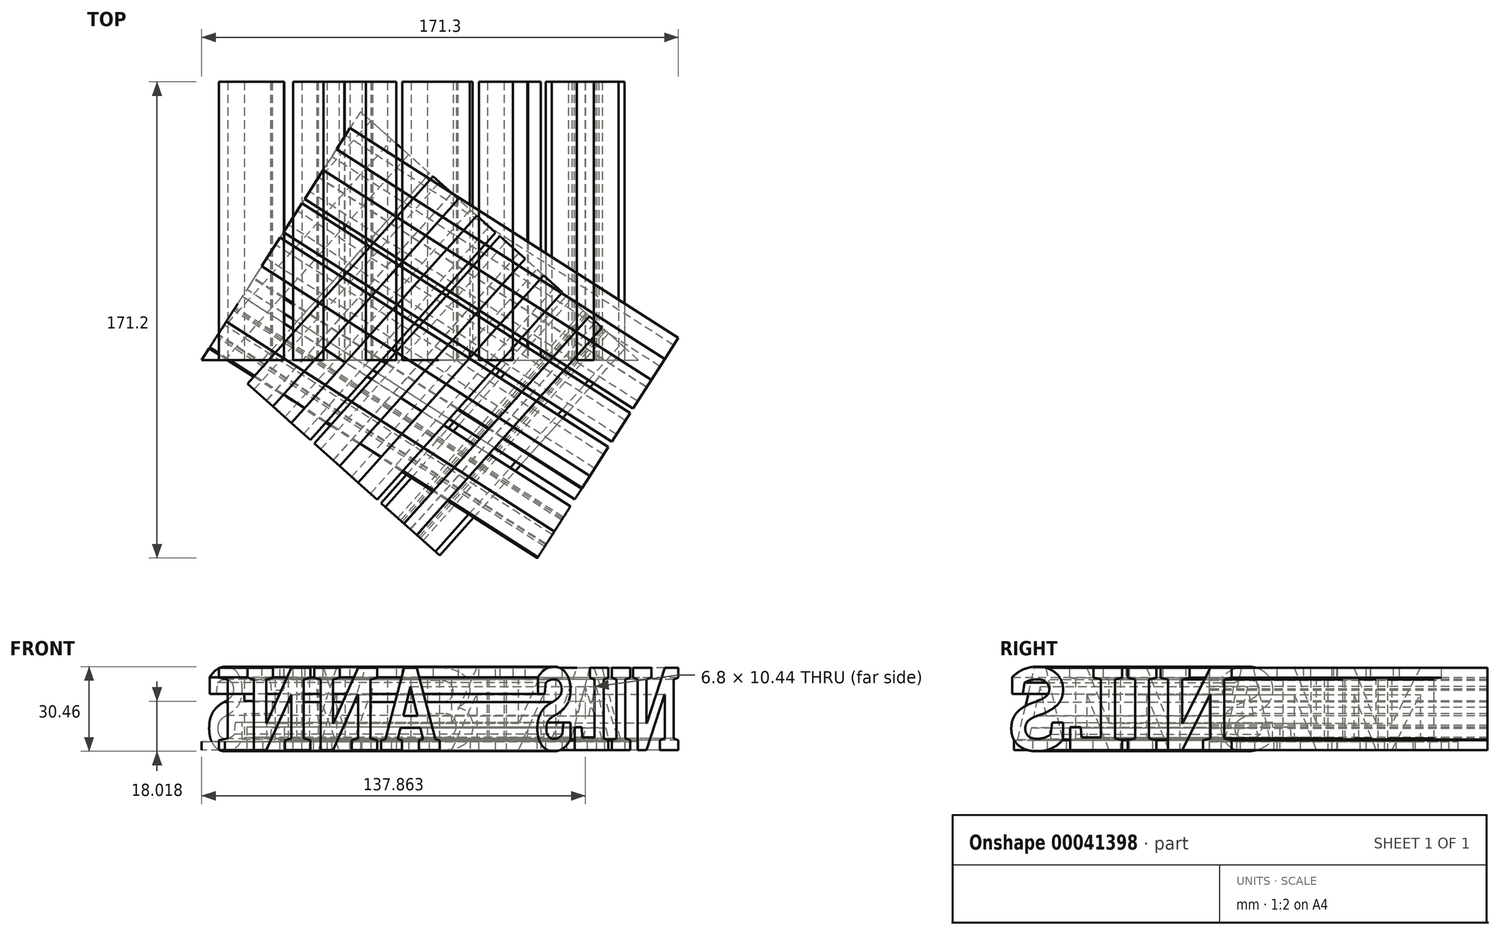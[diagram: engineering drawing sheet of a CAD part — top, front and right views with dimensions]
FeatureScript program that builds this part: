
annotation { "Feature Type Name" : "Feature", "Feature Type Description" : "" }
export const myFeature = defineFeature(function(context is Context, id is Id, definition is map)
    precondition{}
    {
        {
            var Q0;
            Q0=qCreatedBy(makeId("Top.planeOp"),FACE);
            var sketch = newSketch(context, id + "F0", { "sketchPlane" : qUnion([Q0])});
            skLineSegment(sketch, "E0", {"start": v(0, 89.3) * mm, "end": v(-57.1, 0) * mm});
            skLineSegment(sketch, "E1", {"start": v(-57.1, 0) * mm, "end": v(99.9, 0) * mm});
            skLineSegment(sketch, "E2", {"start": v(99.9, 0) * mm, "end": v(0, 89.3) * mm});
            skSolve(sketch);
        }
        {
            var Q0;
            Q0=makeQuery(id+"F0.imprint","IMPRINT",FACE,{"disambiguationData":[TD([[makeQuery(id+"F0.imprint","IMPRINT",EDGE,{"derivedFrom":sQuery(id+"F0.wireOp",EDGE,"E0")}),1.0]])]});
            extrude(context, id + "F1", {"entities" : qUnion([Q0]), "depth" : 3 * mm});
        }
        {
            var Q0;
            Q0=makeQuery(id+"F1.opExtrude","SWEPT_FACE",FACE,{"disambiguationData":[OSD([sQuery(id+"F0.wireOp",EDGE,"E1")])]});
            var sketch = newSketch(context, id + "F2", { "sketchPlane" : qUnion([Q0])});
            skText(sketch, "E3", { "text": "EMBLA", "fontName": "RobotoSlab-Bold.ttf"});
            const initialGuessF2  = {"E3": [-0.05203, 0, 1, 0, 0.03]};
            skSetInitialGuess(sketch, initialGuessF2);
            skSolve(sketch);
        }
        {
            var Q0;
            Q0=makeQuery(id+"F1.opExtrude","SWEPT_FACE",FACE,{"disambiguationData":[OSD([sQuery(id+"F0.wireOp",EDGE,"E2")])]});
            var sketch = newSketch(context, id + "F3", { "sketchPlane" : qUnion([Q0])});
            skText(sketch, "E4", { "text": "ANNA", "fontName": "RobotoSlab-Bold.ttf"});
            const initialGuessF3  = {"E4": [-0.0689, 0, 1, 0, 0.03]};
            skSetInitialGuess(sketch, initialGuessF3);
            skSolve(sketch);
        }
        {
            var Q0;
            Q0=makeQuery(id+"F1.opExtrude","SWEPT_FACE",FACE,{"disambiguationData":[OSD([sQuery(id+"F0.wireOp",EDGE,"E0")])]});
            var sketch = newSketch(context, id + "F4", { "sketchPlane" : qUnion([Q0])});
            skText(sketch, "E5", { "text": "NILS", "fontName": "RobotoSlab-Bold.ttf"});
            const initialGuessF4  = {"E5": [-0.06942, 0, 1, 0, 0.03]};
            skSetInitialGuess(sketch, initialGuessF4);
            skSolve(sketch);
        }
        {
            var Q0;
            Q0 = qSketchRegion(id + "F2", true);
            extrude(context, id + "F5", {"entities" : qUnion([Q0]), "oppositeDirection" : true, "depth" : 100 * mm});
        }
        {
            var Q0;
            Q0 = qSketchRegion(id + "F3", true);
            extrude(context, id + "F6", {"entities" : qUnion([Q0]), "oppositeDirection" : true, "depth" : 100 * mm});
        }
        {
            var Q0;
            Q0 = qSketchRegion(id + "F4", true);
            extrude(context, id + "F7", {"entities" : qUnion([Q0]), "oppositeDirection" : true, "depth" : 140 * mm});
        }
        {
            var Q0;
            Q0=makeQuery(id+"F0.imprint","IMPRINT",FACE,{"disambiguationData":[TD([[makeQuery(id+"F0.imprint","IMPRINT",EDGE,{"derivedFrom":sQuery(id+"F0.wireOp",EDGE,"E0")}),1.0]])]});
            extrude(context, id + "F8", {"entities" : qUnion([Q0]), "depth" : 3 * mm});
        }
        {
            var Q0;
            Q0=makeQuery(id+"F0.imprint","IMPRINT",FACE,{"disambiguationData":[TD([[makeQuery(id+"F0.imprint","IMPRINT",EDGE,{"derivedFrom":sQuery(id+"F0.wireOp",EDGE,"E0")}),1.0]])]});
            extrude(context, id + "F9", {"entities" : qUnion([Q0]), "depth" : 3 * mm});
        }
        {
            var Q0;
            Q0=makeQuery(id+"F6.opExtrude","SWEPT_BODY",BODY,{"disambiguationData":[OSD([sQuery(id+"F3.wireOp",EDGE,"E4.sketch_text.stroke-68"),sQuery(id+"F3.wireOp",EDGE,"E4.sketch_text.stroke-69"),sQuery(id+"F3.wireOp",EDGE,"E4.sketch_text.stroke-70"),sQuery(id+"F3.wireOp",EDGE,"E4.sketch_text.stroke-71"),sQuery(id+"F3.wireOp",EDGE,"E4.sketch_text.stroke-72"),sQuery(id+"F3.wireOp",EDGE,"E4.sketch_text.stroke-73"),sQuery(id+"F3.wireOp",EDGE,"E4.sketch_text.stroke-74"),sQuery(id+"F3.wireOp",EDGE,"E4.sketch_text.stroke-75"),sQuery(id+"F3.wireOp",EDGE,"E4.sketch_text.stroke-76"),sQuery(id+"F3.wireOp",EDGE,"E4.sketch_text.stroke-77"),sQuery(id+"F3.wireOp",EDGE,"E4.sketch_text.stroke-78"),sQuery(id+"F3.wireOp",EDGE,"E4.sketch_text.stroke-79"),sQuery(id+"F3.wireOp",EDGE,"E4.sketch_text.stroke-80"),sQuery(id+"F3.wireOp",EDGE,"E4.sketch_text.stroke-81"),sQuery(id+"F3.wireOp",EDGE,"E4.sketch_text.stroke-82"),sQuery(id+"F3.wireOp",EDGE,"E4.sketch_text.stroke-83"),sQuery(id+"F3.wireOp",EDGE,"E4.sketch_text.stroke-84"),sQuery(id+"F3.wireOp",EDGE,"E4.sketch_text.stroke-85"),sQuery(id+"F3.wireOp",EDGE,"E4.sketch_text.stroke-86"),sQuery(id+"F3.wireOp",EDGE,"E4.sketch_text.stroke-87")])]});
            var Q1;
            Q1=makeQuery(id+"F9.opExtrude","SWEPT_BODY",BODY,{"disambiguationData":[OSD([sQuery(id+"F0.wireOp",EDGE,"E0"),sQuery(id+"F0.wireOp",EDGE,"E1"),sQuery(id+"F0.wireOp",EDGE,"E2")])]});
            var Q2;
            Q2=makeQuery(id+"F8.opExtrude","SWEPT_BODY",BODY,{"disambiguationData":[OSD([sQuery(id+"F0.wireOp",EDGE,"E0"),sQuery(id+"F0.wireOp",EDGE,"E1"),sQuery(id+"F0.wireOp",EDGE,"E2")])]});
            booleanBodies(context, id + "F10", {"operationType" : BooleanOperationType.INTERSECTION, "tools" : qUnion([Q0, Q1, Q2])});
        }
    });
